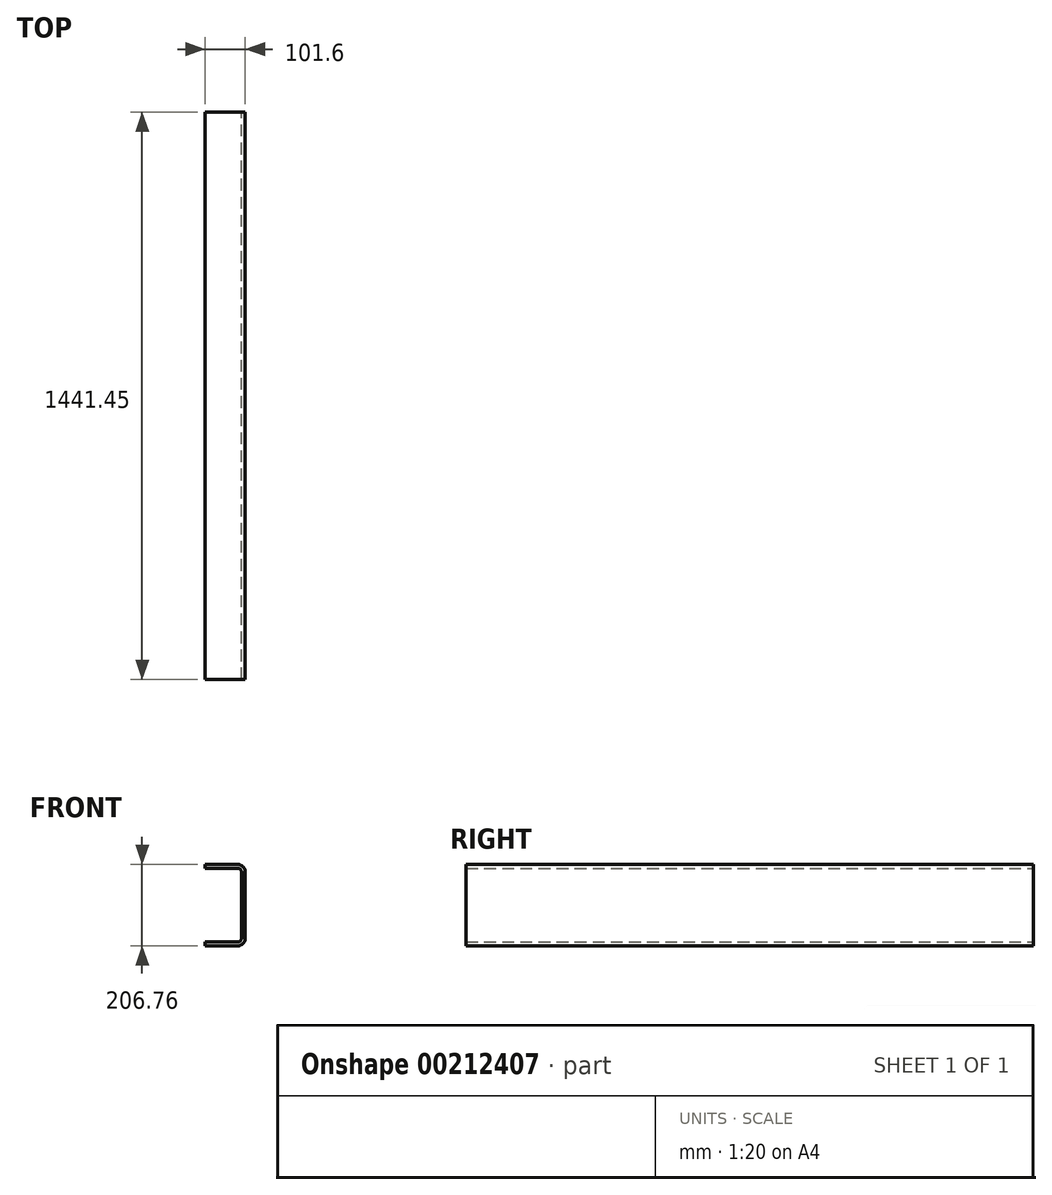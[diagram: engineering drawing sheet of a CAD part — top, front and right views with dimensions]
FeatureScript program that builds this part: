
annotation { "Feature Type Name" : "Feature", "Feature Type Description" : "" }
export const myFeature = defineFeature(function(context is Context, id is Id, definition is map)
    precondition{}
    {
        {
            var Q0;
            Q0=qCreatedBy(makeId("Front.planeOp"),FACE);
            var sketch = newSketch(context, id + "F0", { "sketchPlane" : qUnion([Q0])});
            skLineSegment(sketch, "E0", {"start": v(-19.05, 0) * mm, "end": v(-101.6, 0) * mm});
            skLineSegment(sketch, "E1", {"start": v(-101.6, 0) * mm, "end": v(-101.6, 9.52) * mm});
            skLineSegment(sketch, "E2", {"start": v(-101.6, 9.53) * mm, "end": v(-19.05, 9.53) * mm});
            skLineSegment(sketch, "E3", {"start": v(-9.52, 19.05) * mm, "end": v(-9.52, 187.7) * mm});
            skLineSegment(sketch, "E4", {"start": v(-19.05, 197.23) * mm, "end": v(-101.6, 197.23) * mm});
            skLineSegment(sketch, "E5", {"start": v(-101.6, 197.23) * mm, "end": v(-101.6, 206.76) * mm});
            skLineSegment(sketch, "E6", {"start": v(-101.6, 206.76) * mm, "end": v(-19.05, 206.76) * mm});
            skLineSegment(sketch, "E7", {"start": v(0, 187.7) * mm, "end": v(0, 19.05) * mm});
            skPoint(sketch, "E8.visualSharp", {"position": v(0, 206.76) * mm});
            skArc(sketch, "E8.filletArc", {"start": v(0, 187.7) * mm, "mid": v(-5.58, 201.18) * mm, "end": v(-19.05, 206.76) * mm});
            skPoint(sketch, "E9.visualSharp", {"position": v(-9.53, 197.23) * mm});
            skArc(sketch, "E9.filletArc", {"start": v(-9.52, 187.7) * mm, "mid": v(-12.31, 194.44) * mm, "end": v(-19.05, 197.23) * mm});
            skPoint(sketch, "E10.visualSharp", {"position": v(0, 0) * mm});
            skArc(sketch, "E10.filletArc", {"start": v(-19.05, 0) * mm, "mid": v(-5.58, 5.58) * mm, "end": v(0, 19.05) * mm});
            skPoint(sketch, "E11.visualSharp", {"position": v(-9.52, 9.52) * mm});
            skArc(sketch, "E11.filletArc", {"start": v(-19.05, 9.52) * mm, "mid": v(-12.31, 12.31) * mm, "end": v(-9.52, 19.05) * mm});
            skSolve(sketch);
        }
        {
            var Q0;
            Q0 = qSketchRegion(id + "F0", true);
            extrude(context, id + "F1", {"entities" : qUnion([Q0]), "depth" : 1441.45 * mm});
        }
    });
